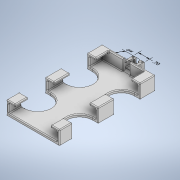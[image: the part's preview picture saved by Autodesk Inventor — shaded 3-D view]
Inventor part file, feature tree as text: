
AUTODESK INVENTOR PART (.ipt)
format: ipt  version: 2020.2 (Build 242310000, 310)  size: 618,496 bytes
history: native  units: in
note: dims shown in document units (in); Inventor stores cm internally (conversion verified against a paired STEP export)
features: sketch x7, extrude x6, fillet x5, other x3, hole x1
ambient origin geometry x8: Origin, YZ Plane, XZ Plane, XY Plane, X Axis, Y Axis, Z Axis, Center Point
bodies: Solid1 (feature_tree)
feature tree (22):
  other  "Annotations"
  extrude  "Extrusion1"  Depth=0.8in
  extrude  "Extrusion2"  Depth=0.5in
  extrude  "Extrusion3"  Depth=0.5in
  extrude  "Extrusion4"  Depth=0.8in
  hole  "Hole1"  [1 undecoded]
  sketch  "Sketch9"  dims[d12=0.15in d13=0.15in]
  extrude  "Extrusion5"  Depth=0.15in
  extrude  "Extrusion6"  Depth=0.3in
  fillet  "Fillet1"  Radius=0.3in
  fillet  "Fillet2"  Radius=0.3in
  fillet  "Fillet3"  Radius=0.3in
  fillet  "Fillet4"  Radius=0.15in
  fillet  "Fillet5"  Radius=0.15in
  sketch  "Sketch1"  dims[d0=3.3in d1=0.8in]
  sketch  "Sketch2"  dims[d2=5.8in d5=0.5in]
  sketch  "Sketch3"  dims[d6=1.0in d7=0.5in]
  sketch  "Sketch5"  dims[d8=1.0in d9=0.8in]
  sketch  "Sketch6"  dims[d10=0.2in d11=0.4in]
  sketch  "Sketch10"  dims[d14=0.77in d15=0.3in d16=0.3in d17=0.3in d18=0.3in d19=0.15in d20=0.15in d21=0.2in d22=0.0in d23=0.15in d24=0.15in d25=0.15in d26=0.15in d27=0.15in d28=0.15in d29=0.15in d30=0.15in d31=0.15in d32=0.09in d33=0.15in d34=0.09in d35=0.68in d36=0.0in d37=0.15in d38=0.0in d39=0.09in d40=0.15in d41=0.09in d42=0.15in d43=0.25in d44=0.0in d45=0.12in d46=0.75in d47=0.375in d48=0.25in d49=0.5635in d50=0.4in d51=0.8108in d55=0.15in d56=0.15in d57=0.15in d58=0.15in d59=0.8in d60=0.15in d61=0.4in d62=0.0in d63=0.4in d64=0.0in d65=0.8in d66=0.05in d67=0.05in d68=0.125in d69=0.05in d70=0.1543in d71=0.3044in d72=0.7in d73=0.2993in d74=0.3805in d75=0.6613in]
  other  "Linear Dimension 1"
  other  "Linear Dimension 2"
note: 1 required parameter value undecoded (feature->parameter linkage not recoverable at this tier; creation-order binding heuristic only, values carry confidence <= 0.55)
